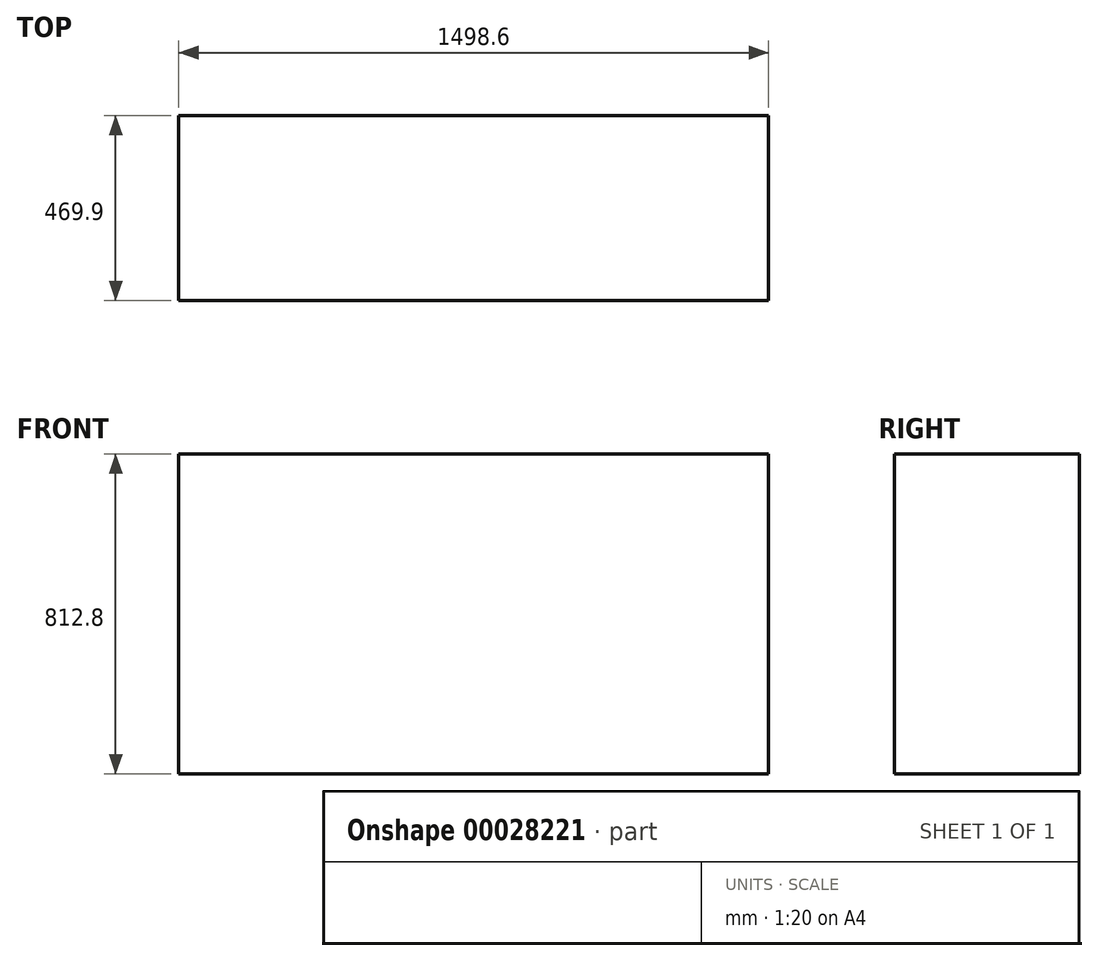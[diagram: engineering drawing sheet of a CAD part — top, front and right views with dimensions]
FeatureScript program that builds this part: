
annotation { "Feature Type Name" : "Feature", "Feature Type Description" : "" }
export const myFeature = defineFeature(function(context is Context, id is Id, definition is map)
    precondition{}
    {
        {
            var Q0;
            Q0=qCreatedBy(makeId("Top.planeOp"),FACE);
            var sketch = newSketch(context, id + "F0", { "sketchPlane" : qUnion([Q0])});
            skLineSegment(sketch, "E0.bottom", {"start": v(-733.85, 105.98) * mm, "end": v(764.75, 105.98) * mm});
            skLineSegment(sketch, "E0.top", {"start": v(-733.85, -363.92) * mm, "end": v(764.75, -363.92) * mm});
            skLineSegment(sketch, "E0.left", {"start": v(-733.85, 105.98) * mm, "end": v(-733.85, -363.92) * mm});
            skLineSegment(sketch, "E0.right", {"start": v(764.75, 105.98) * mm, "end": v(764.75, -363.92) * mm});
            skSolve(sketch);
        }
        {
            var Q0;
            Q0=makeQuery(id+"F0.imprint","IMPRINT",FACE,{"disambiguationData":[TD([[makeQuery(id+"F0.imprint","IMPRINT",EDGE,{"derivedFrom":sQuery(id+"F0.wireOp",EDGE,"E0.bottom")}),-1.0]])]});
            extrude(context, id + "F1", {"entities" : qUnion([Q0]), "depth" : 812.8 * mm});
        }
    });
